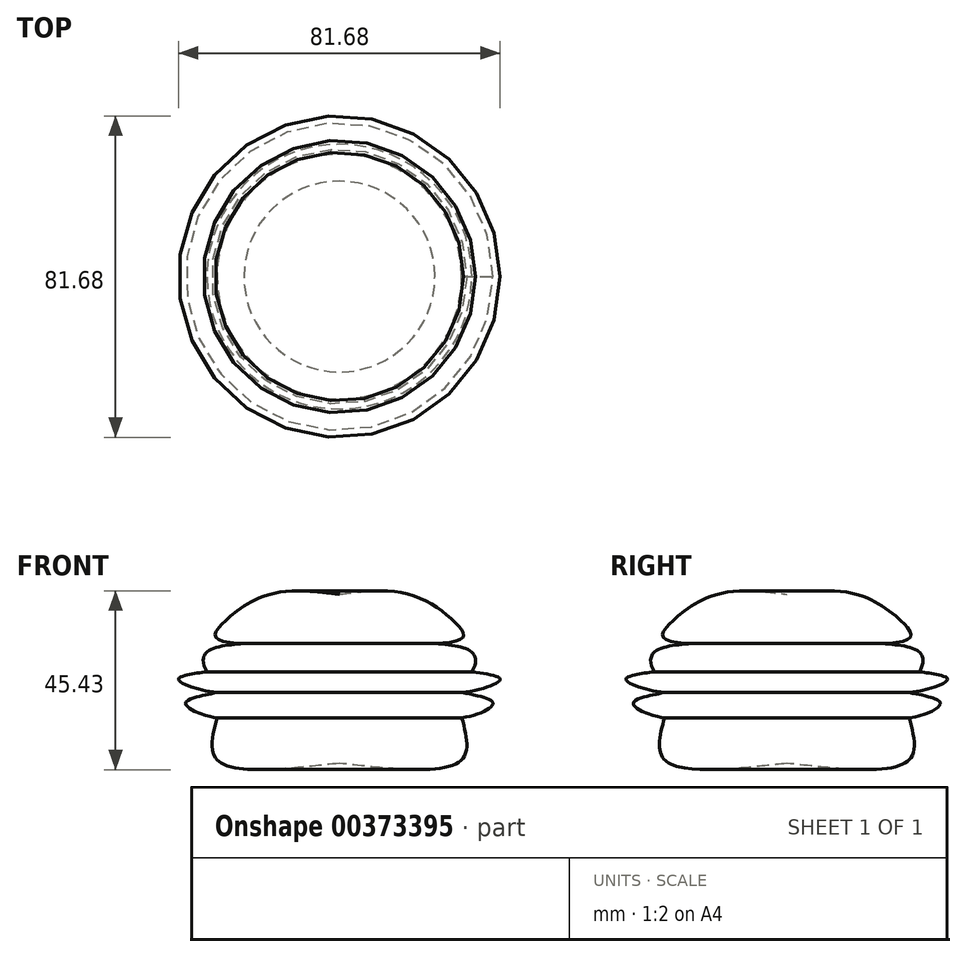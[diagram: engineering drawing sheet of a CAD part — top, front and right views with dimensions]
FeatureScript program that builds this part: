
annotation { "Feature Type Name" : "Feature", "Feature Type Description" : "" }
export const myFeature = defineFeature(function(context is Context, id is Id, definition is map)
    precondition{}
    {
        {
            var Q0;
            Q0=qCreatedBy(makeId("Front.planeOp"),FACE);
            var sketch = newSketch(context, id + "F0", { "sketchPlane" : qUnion([Q0])});
            skFitSpline(sketch, "E0", {"points": [v(0, 56.24) * mm, v(0, -46.18) * mm], "startDerivative": vector(0, -102.41) * mm, "endDerivative": vector(0, -102.41) * mm});
            skFitSpline(sketch, "E1", {"points": [v(0, 56.24) * mm, v(17.68, 56.24) * mm, v(29.26, 49.23) * mm, v(31.4, 45.26) * mm, v(0, 44.65) * mm], "startDerivative": vector(68.58, 8.28) * mm, "endDerivative": vector(-123.73, 7.98) * mm});
            skFitSpline(sketch, "E2", {"points": [v(24.25, 43.7) * mm, v(34.44, 40.39) * mm, v(31.09, 34.6) * mm, v(20.12, 37.95) * mm, v(9.75, 33.99) * mm, v(3.96, 37.95) * mm, v(0, 40.39) * mm], "startDerivative": vector(74.39, -6.45) * mm, "endDerivative": vector(-31.29, 14.58) * mm});
            skFitSpline(sketch, "E3", {"points": [v(33.64, 36.54) * mm, v(40.84, 34.6) * mm, v(31.09, 31.24) * mm, v(14.8, 31.85) * mm, v(0, 31.24) * mm], "startDerivative": vector(54.89, -7.64) * mm, "endDerivative": vector(-53.08, -4.7) * mm});
            skFitSpline(sketch, "E4", {"points": [v(31.09, 31.24) * mm, v(39.01, 28.5) * mm, v(31.09, 24.84) * mm, v(14.8, 25.76) * mm, v(0, 22.1) * mm], "startDerivative": vector(56.21, -10.56) * mm, "endDerivative": vector(-51.43, -18.92) * mm});
            skFitSpline(sketch, "E5", {"points": [v(31.09, 24.84) * mm, v(31.09, 14.17) * mm, v(0, 13.26) * mm], "startDerivative": vector(9.1, -33.95) * mm, "endDerivative": vector(-64.84, 7.2) * mm});
            skLineSegment(sketch, "E6", {"start": v(0, 56.24) * mm, "end": v(0, 13.26) * mm});
            skSolve(sketch);
        }
        {
            var Q0;
            {var subQ0=sQuery(id+"F0.wireOp",EDGE,"E6");var subQ1=sQuery(id+"F0.wireOp",EDGE,"E1");var subQ2=makeQuery(id+"F0.imprint","INTERSECT",VERTEX,{"disambiguationData":[OD(0.0)],"derivedFrom":[subQ1,subQ0]});Q0=makeQuery(id+"F0.imprint","IMPRINT",FACE,{"disambiguationData":[TD([[makeQuery(id+"F0.imprint","IMPRINT",EDGE,{"disambiguationData":[TD([[subQ2,-1.0]])],"derivedFrom":subQ1}),-1.0]])]});}
            var Q1;
            {var subQ0=sQuery(id+"F0.wireOp",EDGE,"E6");var subQ1=sQuery(id+"F0.wireOp",EDGE,"E1");var subQ2=makeQuery(id+"F0.imprint","INTERSECT",VERTEX,{"disambiguationData":[OD(1.0)],"derivedFrom":[subQ1,subQ0]});Q1=makeQuery(id+"F0.imprint","IMPRINT",FACE,{"disambiguationData":[TD([[makeQuery(id+"F0.imprint","IMPRINT",EDGE,{"disambiguationData":[TD([[subQ2,1.0]])],"derivedFrom":subQ1}),1.0]])]});}
            var Q2;
            {var subQ0=sQuery(id+"F0.wireOp",EDGE,"E6");var subQ1=sQuery(id+"F0.wireOp",EDGE,"E2");var subQ2=makeQuery(id+"F0.imprint","INTERSECT",VERTEX,{"derivedFrom":[subQ1,subQ0]});Q2=makeQuery(id+"F0.imprint","IMPRINT",FACE,{"disambiguationData":[TD([[makeQuery(id+"F0.imprint","IMPRINT",EDGE,{"disambiguationData":[TD([[subQ2,1.0]])],"derivedFrom":subQ1}),1.0]])]});}
            var Q3;
            {var subQ0=sQuery(id+"F0.wireOp",EDGE,"E6");var subQ1=sQuery(id+"F0.wireOp",EDGE,"E3");var subQ2=makeQuery(id+"F0.imprint","INTERSECT",VERTEX,{"derivedFrom":[subQ1,subQ0]});Q3=makeQuery(id+"F0.imprint","IMPRINT",FACE,{"disambiguationData":[TD([[makeQuery(id+"F0.imprint","IMPRINT",EDGE,{"disambiguationData":[TD([[subQ2,1.0]])],"derivedFrom":subQ1}),1.0]])]});}
            var Q4;
            {var subQ3=sQuery(id+"F0.wireOp",EDGE,"E5");Q4=makeQuery(id+"F0.imprint","IMPRINT",FACE,{"disambiguationData":[TD([[makeQuery(id+"F0.imprint","IMPRINT",EDGE,{"derivedFrom":subQ3}),-1.0]])]});}
            var Q5;
            Q5=sQuery(id+"F0.wireOp",EDGE,"E6");
            revolve(context, id + "F1", {"entities" : qUnion([Q0, Q1, Q2, Q3, Q4]), "axis" : qUnion([Q5]), "revolveType" : RevolveType.FULL});
        }
    });
